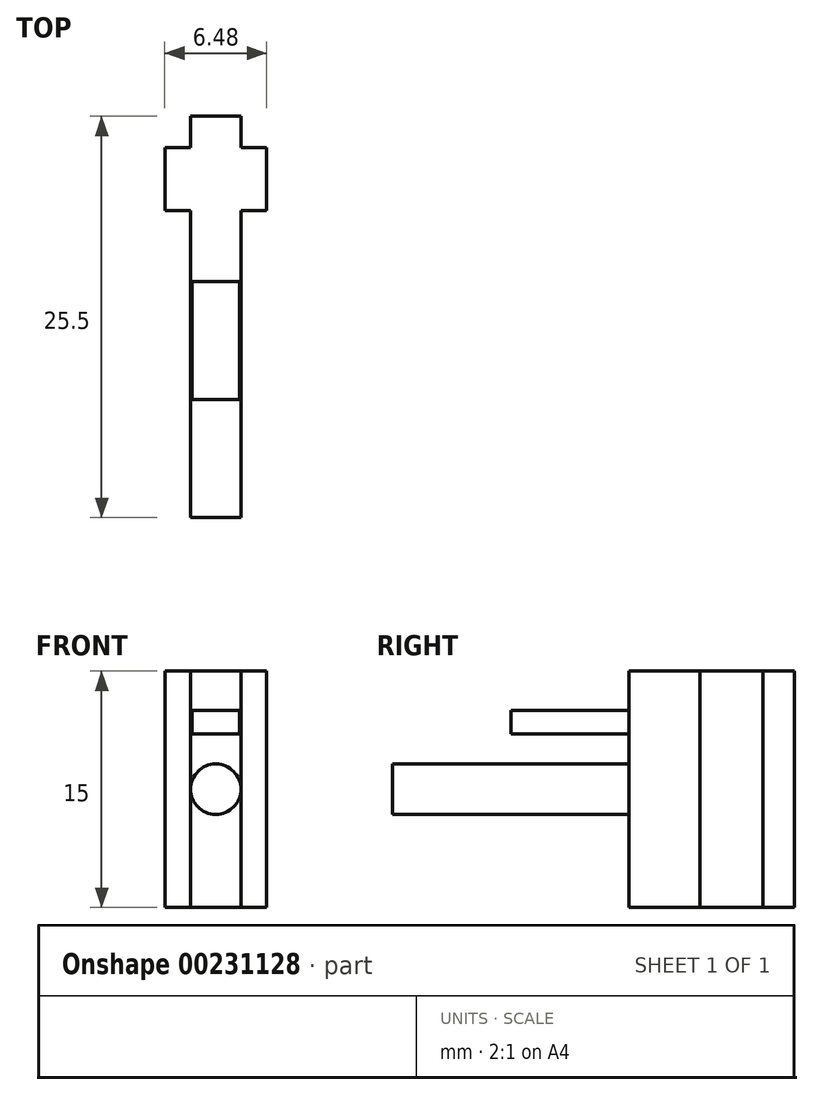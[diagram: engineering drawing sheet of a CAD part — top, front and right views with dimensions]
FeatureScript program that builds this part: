
annotation { "Feature Type Name" : "Feature", "Feature Type Description" : "" }
export const myFeature = defineFeature(function(context is Context, id is Id, definition is map)
    precondition{}
    {
        {
            var Q0;
            Q0=qCreatedBy(makeId("Top.planeOp"),FACE);
            var sketch = newSketch(context, id + "F0", { "sketchPlane" : qUnion([Q0])});
            skLineSegment(sketch, "E0", {"start": v(0, 0) * mm, "end": v(0, 10.5) * mm, "construction": true});
            skLineSegment(sketch, "E1", {"start": v(0, 10.5) * mm, "end": v(-1.6, 10.5) * mm});
            skLineSegment(sketch, "E2", {"start": v(-1.6, 10.5) * mm, "end": v(-1.6, 8.5) * mm});
            skLineSegment(sketch, "E3", {"start": v(-1.6, 8.5) * mm, "end": v(-3.24, 8.5) * mm});
            skLineSegment(sketch, "E4", {"start": v(-3.24, 8.5) * mm, "end": v(-3.24, 4.5) * mm});
            skLineSegment(sketch, "E5", {"start": v(-3.24, 4.5) * mm, "end": v(-1.6, 4.5) * mm});
            skLineSegment(sketch, "E6", {"start": v(-1.6, 4.5) * mm, "end": v(-1.6, 0) * mm});
            skLineSegment(sketch, "E7", {"start": v(-1.6, 0) * mm, "end": v(0, 0) * mm});
            skLineSegment(sketch, "E8.MirrorCS", {"start": v(0, 10.5) * mm, "end": v(1.6, 10.5) * mm});
            skLineSegment(sketch, "E9.MirrorCS", {"start": v(1.6, 10.5) * mm, "end": v(1.6, 8.5) * mm});
            skLineSegment(sketch, "E10.MirrorCS", {"start": v(3.24, 4.5) * mm, "end": v(1.6, 4.5) * mm});
            skLineSegment(sketch, "E11.MirrorCS", {"start": v(1.6, 4.5) * mm, "end": v(1.6, 0) * mm});
            skLineSegment(sketch, "E12.MirrorCS", {"start": v(3.24, 8.5) * mm, "end": v(3.24, 4.5) * mm});
            skLineSegment(sketch, "E13.MirrorCS", {"start": v(1.6, 0) * mm, "end": v(0, 0) * mm});
            skLineSegment(sketch, "E14.MirrorCS", {"start": v(1.6, 8.5) * mm, "end": v(3.24, 8.5) * mm});
            skSolve(sketch);
        }
        {
            var Q0;
            Q0=makeQuery(id+"F0.imprint","IMPRINT",FACE,{"disambiguationData":[TD([[makeQuery(id+"F0.imprint","IMPRINT",EDGE,{"derivedFrom":sQuery(id+"F0.wireOp",EDGE,"E1")}),1.0]])]});
            extrude(context, id + "F1", {"entities" : qUnion([Q0]), "endBound" : BoundingType.SYMMETRIC, "oppositeDirection" : true, "depth" : 15 * mm});
        }
        {
            var Q0;
            Q0=qCreatedBy(makeId("Front.planeOp"),FACE);
            var sketch = newSketch(context, id + "F2", { "sketchPlane" : qUnion([Q0])});
            skCircle(sketch, "E15", {"center": v(0, 0) * mm, "radius": 1.6 * mm});
            skSolve(sketch);
        }
        {
            var Q0;
            Q0=makeQuery(id+"F2.imprint","IMPRINT",FACE,{"disambiguationData":[TD([[makeQuery(id+"F2.imprint","IMPRINT",EDGE,{"derivedFrom":sQuery(id+"F2.wireOp",EDGE,"E15")}),1.0]])]});
            extrude(context, id + "F3", {"entities" : qUnion([Q0]), "operationType" : NewBodyOperationType.ADD, "depth" : 15 * mm});
        }
        {
            var Q0;
            Q0=qCreatedBy(makeId("Front.planeOp"),FACE);
            var sketch = newSketch(context, id + "F4", { "sketchPlane" : qUnion([Q0])});
            skLineSegment(sketch, "E16.bottom", {"start": v(1.5, 3.5) * mm, "end": v(-1.5, 3.5) * mm});
            skLineSegment(sketch, "E16.top", {"start": v(1.5, 5) * mm, "end": v(-1.5, 5) * mm});
            skLineSegment(sketch, "E16.left", {"start": v(1.5, 3.5) * mm, "end": v(1.5, 5) * mm});
            skLineSegment(sketch, "E16.right", {"start": v(-1.5, 3.5) * mm, "end": v(-1.5, 5) * mm});
            skPoint(sketch, "E16.middle", {"position": v(0, 4.25) * mm});
            skSolve(sketch);
        }
        {
            var Q0;
            Q0=qSketchRegion(id+"F4",true);
            extrude(context, id + "F5", {"entities" : qUnion([Q0]), "endBound" : BoundingType.SYMMETRIC, "depth" : 15 * mm});
        }
        {
            var Q0;
            Q0=qCreatedBy(makeId("Top.planeOp"),FACE);
            var sketch = newSketch(context, id + "F6", { "sketchPlane" : qUnion([Q0])});
            skLineSegment(sketch, "E17.bottom", {"start": v(1.5, 3.5) * mm, "end": v(-1.5, 3.5) * mm});
            skLineSegment(sketch, "E17.top", {"start": v(1.5, 5) * mm, "end": v(-1.5, 5) * mm});
            skLineSegment(sketch, "E17.left", {"start": v(1.5, 3.5) * mm, "end": v(1.5, 5) * mm});
            skLineSegment(sketch, "E17.right", {"start": v(-1.5, 3.5) * mm, "end": v(-1.5, 5) * mm});
            skPoint(sketch, "E17.middle", {"position": v(0, 4.25) * mm});
            skSolve(sketch);
        }
        {
            var Q0;
            Q0=qSketchRegion(id+"F6",true);
            extrude(context, id + "F7", {"entities" : qUnion([Q0]), "operationType" : NewBodyOperationType.ADD, "endBound" : BoundingType.SYMMETRIC, "depth" : 15 * mm});
        }
    });
